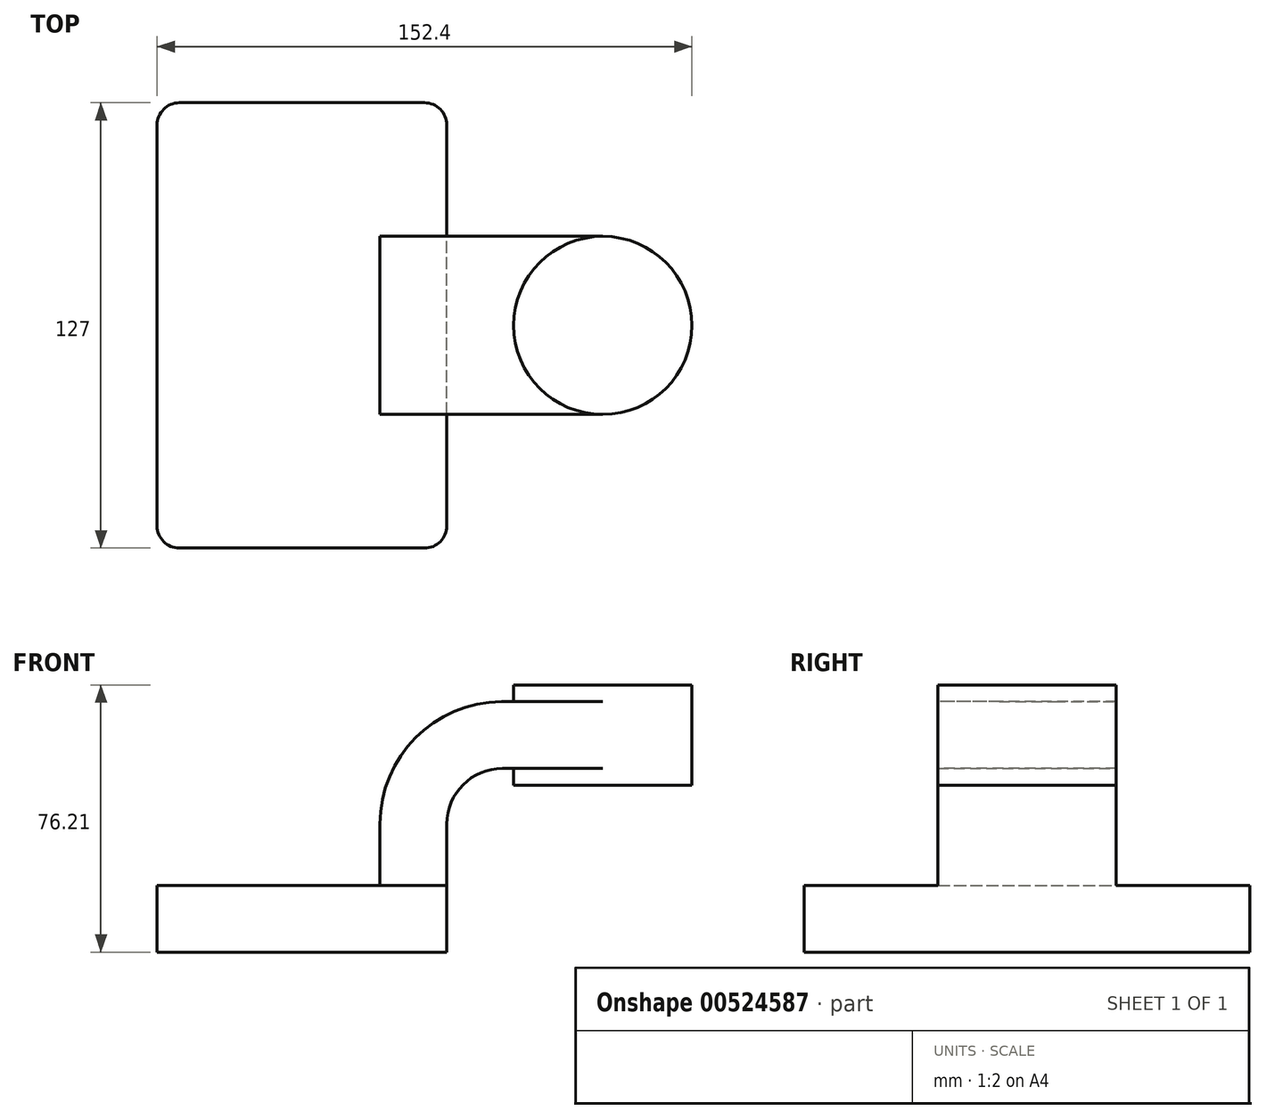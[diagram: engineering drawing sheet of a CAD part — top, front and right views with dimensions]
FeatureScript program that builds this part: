
annotation { "Feature Type Name" : "Feature", "Feature Type Description" : "" }
export const myFeature = defineFeature(function(context is Context, id is Id, definition is map)
    precondition{}
    {
        {
            var Q0;
            Q0=qCreatedBy(makeId("Front.planeOp"),FACE);
            var sketch = newSketch(context, id + "F0", { "sketchPlane" : qUnion([Q0])});
            skLineSegment(sketch, "E0.bottom", {"start": v(-41.28, 9.53) * mm, "end": v(41.28, 9.53) * mm});
            skLineSegment(sketch, "E0.top", {"start": v(-41.28, -9.52) * mm, "end": v(41.28, -9.52) * mm});
            skLineSegment(sketch, "E0.left", {"start": v(-41.28, 9.53) * mm, "end": v(-41.28, -9.52) * mm});
            skLineSegment(sketch, "E0.right", {"start": v(41.28, 9.53) * mm, "end": v(41.28, -9.52) * mm});
            skPoint(sketch, "E0.middle", {"position": v(0, 0) * mm});
            skPoint(sketch, "E1.middle", {"position": v(-41.28, 9.53) * mm});
            skLineSegment(sketch, "E2.bottom", {"start": v(111.12, 38.1) * mm, "end": v(60.33, 38.1) * mm});
            skLineSegment(sketch, "E2.top", {"start": v(111.12, 66.68) * mm, "end": v(60.33, 66.68) * mm});
            skLineSegment(sketch, "E2.left", {"start": v(111.12, 38.1) * mm, "end": v(111.12, 66.68) * mm});
            skLineSegment(sketch, "E2.right", {"start": v(60.33, 38.1) * mm, "end": v(60.33, 66.68) * mm});
            skPoint(sketch, "E2.middle", {"position": v(85.72, 52.39) * mm});
            skLineSegment(sketch, "E3", {"start": v(41.28, 9.53) * mm, "end": v(41.28, 26.99) * mm});
            skArc(sketch, "E4", {"start": v(41.28, 26.99) * mm, "mid": v(45.92, 38.21) * mm, "end": v(57.15, 42.86) * mm});
            skLineSegment(sketch, "E5", {"start": v(57.15, 42.86) * mm, "end": v(85.72, 42.86) * mm});
            skLineSegment(sketch, "E6.0", {"start": v(57.15, 61.91) * mm, "end": v(85.72, 61.91) * mm});
            skArc(sketch, "E6.1", {"start": v(22.23, 26.99) * mm, "mid": v(32.45, 51.68) * mm, "end": v(57.15, 61.91) * mm});
            skLineSegment(sketch, "E6.2", {"start": v(22.23, 9.53) * mm, "end": v(22.23, 26.99) * mm});
            skFitSpline(sketch, "E7", {"points": [v(-41.28, 9.52) * mm, v(57.15, 61.91) * mm], "startDerivative": vector(0.56, 76.5) * mm, "endDerivative": vector(219.14, 0.74) * mm});
            skLineSegment(sketch, "E8", {"start": v(85.72, 66.68) * mm, "end": v(85.72, 38.1) * mm});
            skSolve(sketch);
        }
        {
            var Q0;
            Q0=makeQuery(id+"F0.imprint","IMPRINT",FACE,{"disambiguationData":[TD([[makeQuery(id+"F0.imprint","IMPRINT",EDGE,{"derivedFrom":sQuery(id+"F0.wireOp",EDGE,"E0.top")}),1.0]])]});
            extrude(context, id + "F1", {"entities" : qUnion([Q0]), "endBound" : BoundingType.SYMMETRIC, "depth" : 127 * mm, "offsetDistance" : 25.4 * mm});
        }
        {
            var Q0;
            {var subQ1=sQuery(id+"F0.wireOp",EDGE,"E3");Q0=makeQuery(id+"F0.imprint","IMPRINT",FACE,{"disambiguationData":[TD([[makeQuery(id+"F0.imprint","IMPRINT",EDGE,{"derivedFrom":subQ1}),1.0]])]});}
            var Q1;
            {var subQ0=sQuery(id+"F0.wireOp",EDGE,"E5");var subQ1=sQuery(id+"F0.wireOp",EDGE,"E2.right");var subQ2=makeQuery(id+"F0.imprint","INTERSECT",VERTEX,{"derivedFrom":[subQ1,subQ0]});Q1=makeQuery(id+"F0.imprint","IMPRINT",FACE,{"disambiguationData":[TD([[makeQuery(id+"F0.imprint","IMPRINT",EDGE,{"disambiguationData":[TD([[subQ2,-1.0]])],"derivedFrom":subQ1}),-1.0]])]});}
            extrude(context, id + "F2", {"entities" : qUnion([Q0, Q1]), "operationType" : NewBodyOperationType.ADD, "endBound" : BoundingType.SYMMETRIC, "depth" : 50.8 * mm, "offsetDistance" : 25.4 * mm});
        }
        {
            var Q0;
            {var subQ4=sQuery(id+"F0.wireOp",EDGE,"E6.1");Q0=makeQuery(id+"F0.imprint","IMPRINT",FACE,{"disambiguationData":[TD([[makeQuery(id+"F0.imprint","IMPRINT",EDGE,{"derivedFrom":subQ4}),1.0]])]});}
            extrude(context, id + "F3", {"entities" : qUnion([Q0]), "operationType" : NewBodyOperationType.ADD, "endBound" : BoundingType.SYMMETRIC, "depth" : 15.88 * mm, "offsetDistance" : 25.4 * mm});
        }
        {
            var Q0;
            {var subQ4=sQuery(id+"F0.wireOp",EDGE,"E2.left");Q0=makeQuery(id+"F0.imprint","IMPRINT",FACE,{"disambiguationData":[TD([[makeQuery(id+"F0.imprint","IMPRINT",EDGE,{"derivedFrom":subQ4}),1.0]])]});}
            var Q1;
            Q1=sQuery(id+"F0.wireOp",EDGE,"E8");
            revolve(context, id + "F4", {"operationType" : NewBodyOperationType.ADD, "entities" : qUnion([Q0]), "axis" : qUnion([Q1]), "revolveType" : RevolveType.FULL});
        }
        {
            var Q0;
            Q0=makeQuery(id+"F1.opExtrude","CAP_EDGE",EDGE,{"disambiguationData":[OSD([sQuery(id+"F0.wireOp",EDGE,"E0.right")])],"isStart":false});
            var Q1;
            Q1=makeQuery(id+"F1.opExtrude","CAP_EDGE",EDGE,{"disambiguationData":[OSD([sQuery(id+"F0.wireOp",EDGE,"E0.left")])],"isStart":false});
            var Q2;
            Q2=makeQuery(id+"F1.opExtrude","CAP_EDGE",EDGE,{"disambiguationData":[OSD([sQuery(id+"F0.wireOp",EDGE,"E0.right")])],"isStart":true});
            var Q3;
            Q3=makeQuery(id+"F1.opExtrude","CAP_EDGE",EDGE,{"disambiguationData":[OSD([sQuery(id+"F0.wireOp",EDGE,"E0.left")])],"isStart":true});
            fillet(context, id + "F5", {"entities" : qUnion([Q0, Q1, Q2, Q3]), "radius" : 6.35 * mm, "tangentPropagation" : true, "allowEdgeOverflow" : false});
        }
    });
